# Revit family: CADS_AIRFLOWdev_AirflexPro_Round_DistributionBox_15PortExt
name_source: partatom
category: Duct Accessories
units: mm (PartAtom-declared; Revit-internal decimal feet)

## family parameters
Always vertical = Yes
Cut with Voids When Loaded = No
OmniClass Number = 23.75.00.00
OmniClass Title = Climate Control (HVAC)
Part Type = Breaks Into
Round Connector Dimension = Use Diameter
Shared = No
Work Plane-Based = No

## types (2) — shared parameters
6MonthlyMaintenance = Visually inspect system, clean the fan and ducting if necessary
AirflowRateRange = 135.0 L/s
AssemblyPlace = UNKNOWN
AssetType = FIXED
CEApproval = Yes
Color = Silver
Conn_IDia = 180 mm  [stored 0.590551 ft]
Constituents = 15-Port inline / 90o option distribution box. Round spigots & sound attenuation fitted.
DurationUnit = Year
ExpectedServiceLife = 10
Features = 15-Port inline / 90o option distribution box. Round spigots & sound attenuation fitted.
Finish = Lacquer
FireControlPanelLinks = No
Fitting Type = Ignore
Grade = Stainless
GrossWeight = 11.25 kg
Halfb1 = 250 mm  [stored 0.82021 ft]
ISO140001 = Yes
ISO90001 = Yes
IsExtendedWarranty = No
LongitudinalSeam = None
Manufacturer = Airflow Developments Ltd
ManufacturerAddress = Aidelle House
Lancaster Road
Cressex Business Park
High Wycombe
Bucks
HP123QP
ManufacturerTelephone = 01494 525252
ManufacturerWebsite = www.airflow.com
Material = Steel
NBSCode = 45-80-50/394 Ventilation ducts
NominalHeight = 470 mm
NominalLength = 160 mm  [stored 0.524934 ft]
NominalWidth = 530 mm
PassiveHouseApproval = No
PointOfContact = Airflow Developments Ltd
ProductLiterature = https://www.airflow.com
ProductionYear = 2017
Quantity = 1
RedDotDesignAward = No
ReplacementCost = 377.244
SAPApproval = Yes
ServiceLifeDuration = 10
ServiceLifeType = EXPECTEDSERVICELIFE
Shape = Rectangular
ShippingWeight = 13.50 kg
Size = 160 x 530 x 470
Status = New
TemperatureRange = up to 40°C
Uniclass2015 = Pr_30_59_96_92:Ventilation ducts
WarrantyGuarantor = Airflow Developments Ltd
WarrantyPeriod = 0
WorkingPressure = 3000.0 Pa
b1 = 500 mm  [stored 1.64042 ft]
h1 = 300 mm
l1 = 600 mm
zero-valued in all types: CADS_Index

## type names (no varying parameters)
- CADS_AIRFLOWdev_AirflexPro_Round_DistributionBox_15Port
- CADS_AIRFLOWdev_AirflexPro_Round_DistributionBox_15Port EXT

note: [stored X ft] marks values corroborated as IEEE doubles in the binary element streams (Revit-internal decimal feet)

## geometry (parser evidence)
native form markers: Blend x6, Sweep x27
no freeform markers — native parametric forms only
